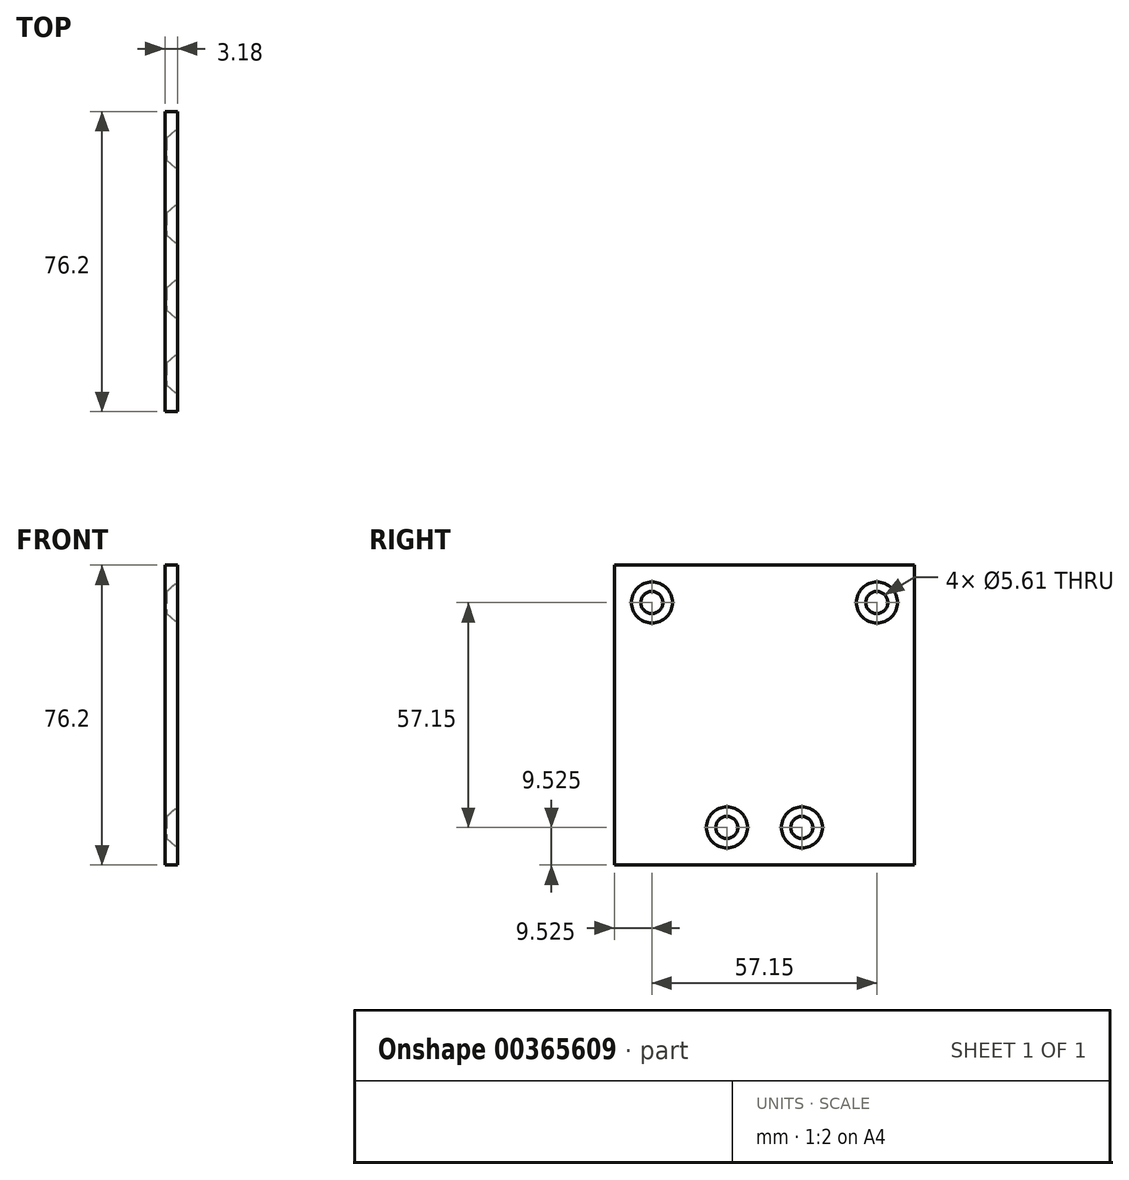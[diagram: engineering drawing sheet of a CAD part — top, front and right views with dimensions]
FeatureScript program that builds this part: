
annotation { "Feature Type Name" : "Feature", "Feature Type Description" : "" }
export const myFeature = defineFeature(function(context is Context, id is Id, definition is map)
    precondition{}
    {
        {
            var Q0;
            Q0=qCreatedBy(makeId("Right.planeOp"),FACE);
            var sketch = newSketch(context, id + "F0", { "sketchPlane" : qUnion([Q0])});
            skLineSegment(sketch, "E0.bottom", {"start": v(38.1, -38.1) * mm, "end": v(-38.1, -38.1) * mm});
            skLineSegment(sketch, "E0.top", {"start": v(38.1, 38.1) * mm, "end": v(-38.1, 38.1) * mm});
            skLineSegment(sketch, "E0.left", {"start": v(38.1, -38.1) * mm, "end": v(38.1, 38.1) * mm});
            skLineSegment(sketch, "E0.right", {"start": v(-38.1, -38.1) * mm, "end": v(-38.1, 38.1) * mm});
            skPoint(sketch, "E0.middle", {"position": v(0, 0) * mm});
            skSolve(sketch);
        }
        {
            var Q0;
            Q0=qSketchRegion(id+"F0",true);
            extrude(context, id + "F1", {"entities" : qUnion([Q0]), "depth" : 3.17 * mm, "offsetDistance" : 25.4 * mm});
        }
        {
            var Q0;
            Q0=makeQuery(id+"F1.opExtrude","CAP_FACE",FACE,{"disambiguationData":[OSD([sQuery(id+"F0.wireOp",EDGE,"E0.bottom"),sQuery(id+"F0.wireOp",EDGE,"E0.top"),sQuery(id+"F0.wireOp",EDGE,"E0.left"),sQuery(id+"F0.wireOp",EDGE,"E0.right")])],"isStart":false});
            var sketch = newSketch(context, id + "F2", { "sketchPlane" : qUnion([Q0])});
            skPoint(sketch, "E1", {"position": v(-28.58, 28.57) * mm});
            skPoint(sketch, "E2", {"position": v(28.57, 28.58) * mm});
            skPoint(sketch, "E3", {"position": v(9.53, -28.58) * mm});
            skPoint(sketch, "E4", {"position": v(-9.52, -28.58) * mm});
            skSolve(sketch);
        }
        {
            var Q0;
            Q0=sQuery(id+"F2.wireOp",VERTEX,"E1");
            var Q1;
            Q1=sQuery(id+"F2.wireOp",VERTEX,"E2");
            var Q2;
            Q2=sQuery(id+"F2.wireOp",VERTEX,"E3");
            var Q3;
            Q3=sQuery(id+"F2.wireOp",VERTEX,"E4");
            var Q4;
            Q4=makeQuery(id+"F1.opExtrude","SWEPT_BODY",BODY,{"disambiguationData":[OSD([sQuery(id+"F0.wireOp",EDGE,"E0.bottom"),sQuery(id+"F0.wireOp",EDGE,"E0.top"),sQuery(id+"F0.wireOp",EDGE,"E0.left"),sQuery(id+"F0.wireOp",EDGE,"E0.right")])]});
            hole(context, id + "F3", {"style" : HoleStyle.C_SINK, "endStyle" : HoleEndStyle.THROUGH, "standardTappedOrClearance" : lookupTablePath({ "fit" : "Normal (ASME)", "standard" : "ANSI", "size" : "#10", "type" : "Clearance" }), "standardBlindInLast" : lookupTablePath({ "fit" : "Normal", "standard" : "ANSI", "engagement" : "75%", "pitch" : "24 tpi", "size" : "#10", "type" : "Clearance & tapped" }), "holeDiameter" : 5.61 * mm, "cSinkDiameter" : 10.44 * mm, "cSinkAngle" : 82 * degree, "majorDiameter" : 6.35 * mm, "isTappedThrough" : true, "tappedDepth" : 12.7 * mm, "tapClearance" : 3, "locations" : qUnion([Q0, Q1, Q2, Q3]), "scope" : qUnion([Q4]), "startStyle" : HoleStartStyle.SKETCH});
        }
    });
